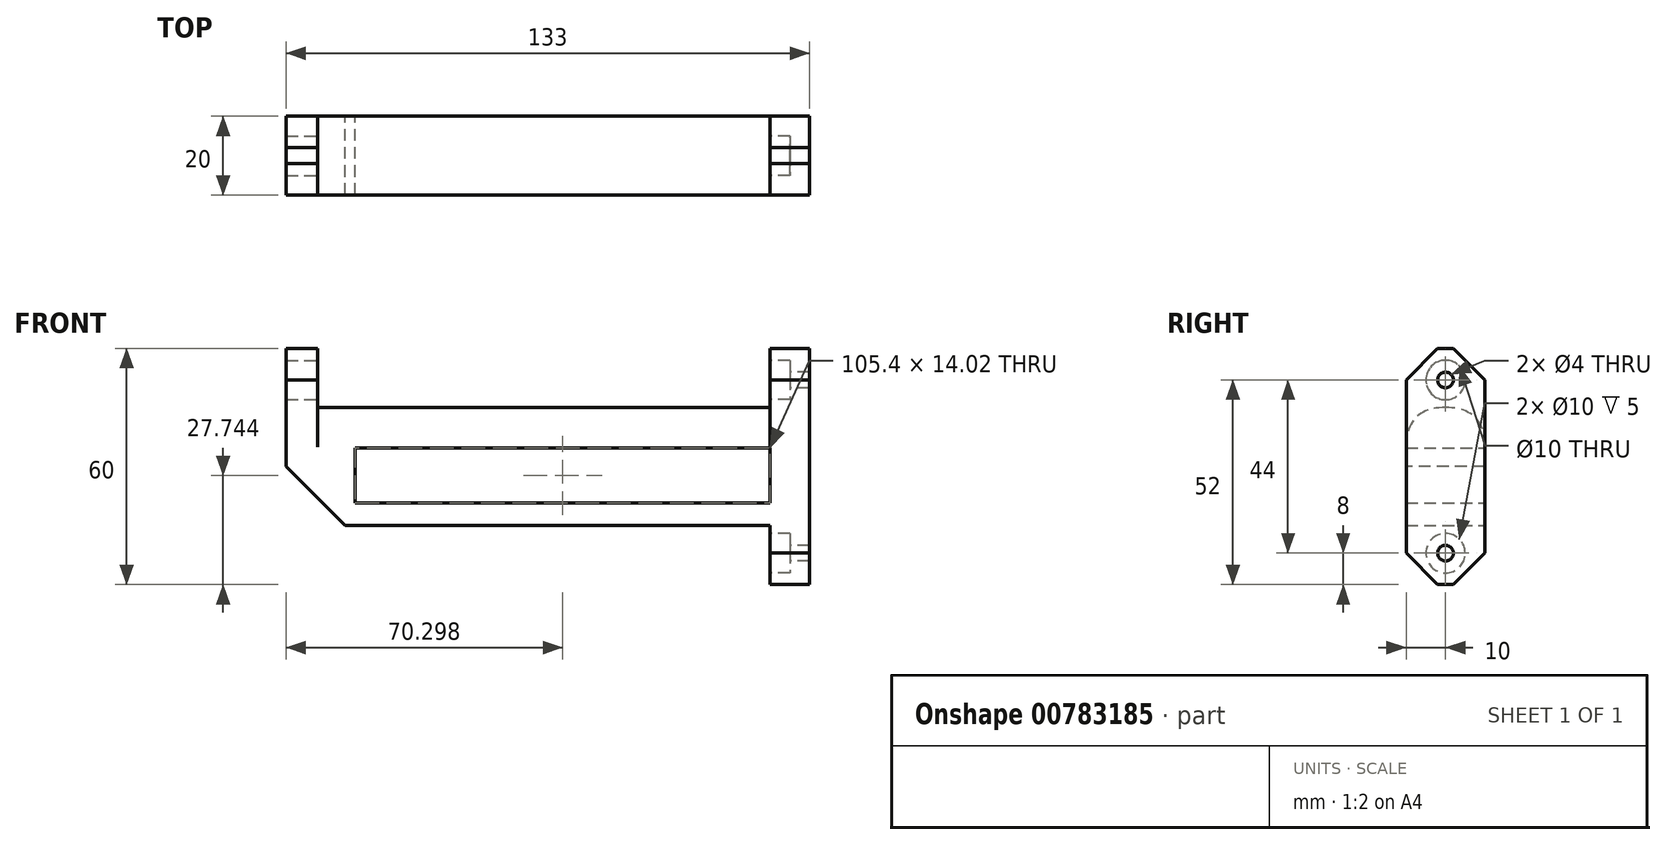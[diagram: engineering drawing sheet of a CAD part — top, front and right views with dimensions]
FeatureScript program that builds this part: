
annotation { "Feature Type Name" : "Feature", "Feature Type Description" : "" }
export const myFeature = defineFeature(function(context is Context, id is Id, definition is map)
    precondition{}
    {
        {
            var Q0;
            Q0=qCreatedBy(makeId("Front.planeOp"),FACE);
            var sketch = newSketch(context, id + "F0", { "sketchPlane" : qUnion([Q0])});
            skLineSegment(sketch, "E0.bottom", {"start": v(57.5, 15) * mm, "end": v(-57.5, 15) * mm});
            skLineSegment(sketch, "E0.top", {"start": v(57.5, -15) * mm, "end": v(-57.5, -15) * mm});
            skLineSegment(sketch, "E0.left", {"start": v(57.5, 15) * mm, "end": v(57.5, -15) * mm});
            skLineSegment(sketch, "E0.right", {"start": v(-57.5, 15) * mm, "end": v(-57.5, -15) * mm});
            skPoint(sketch, "E0.middle", {"position": v(0, 0) * mm});
            skLineSegment(sketch, "E1.bottom", {"start": v(-57.5, -15) * mm, "end": v(-65.5, -15) * mm});
            skLineSegment(sketch, "E1.top", {"start": v(-57.5, 30) * mm, "end": v(-65.5, 30) * mm});
            skLineSegment(sketch, "E1.left", {"start": v(-57.5, -15) * mm, "end": v(-57.5, 30) * mm});
            skLineSegment(sketch, "E1.right", {"start": v(-65.5, -15) * mm, "end": v(-65.5, 30) * mm});
            skLineSegment(sketch, "E2", {"start": v(57.5, 15) * mm, "end": v(57.5, 30) * mm});
            skLineSegment(sketch, "E3", {"start": v(57.5, 30) * mm, "end": v(67.5, 30) * mm});
            skLineSegment(sketch, "E4", {"start": v(67.5, 30) * mm, "end": v(67.5, 15) * mm});
            skLineSegment(sketch, "E5", {"start": v(67.5, 15) * mm, "end": v(67.5, -15) * mm});
            skLineSegment(sketch, "E6", {"start": v(67.5, -15) * mm, "end": v(67.5, -30) * mm});
            skLineSegment(sketch, "E7", {"start": v(67.5, -30) * mm, "end": v(57.5, -30) * mm});
            skLineSegment(sketch, "E8", {"start": v(57.5, -30) * mm, "end": v(57.5, -15) * mm});
            skLineSegment(sketch, "E9.bottom", {"start": v(57.5, -9.26) * mm, "end": v(-47.9, -9.26) * mm});
            skLineSegment(sketch, "E9.top", {"start": v(57.5, 4.75) * mm, "end": v(-47.9, 4.75) * mm});
            skLineSegment(sketch, "E9.left", {"start": v(57.5, -9.26) * mm, "end": v(57.5, 4.75) * mm});
            skLineSegment(sketch, "E9.right", {"start": v(-47.9, -9.26) * mm, "end": v(-47.9, 4.75) * mm});
            skSolve(sketch);
        }
        {
            var Q0;
            Q0 = qSketchRegion(id + "F0", true);
            extrude(context, id + "F1", {"entities" : qUnion([Q0]), "endBound" : BoundingType.SYMMETRIC, "depth" : 20 * mm, "offsetDistance" : 25 * mm});
        }
        {
            var Q0;
            Q0=makeQuery(id+"F1.opExtrude","CAP_EDGE",EDGE,{"disambiguationData":[OSD([sQuery(id+"F0.wireOp",EDGE,"E0.bottom")])],"isStart":false});
            var Q1;
            Q1=makeQuery(id+"F1.opExtrude","CAP_EDGE",EDGE,{"disambiguationData":[OSD([sQuery(id+"F0.wireOp",EDGE,"E0.bottom")])],"isStart":true});
            fillet(context, id + "F2", {"entities" : qUnion([Q0, Q1]), "radius" : 10 * mm, "rho" : 0.5, "crossSection" : FilletCrossSection.CONIC, "allowEdgeOverflow" : false});
        }
        {
            var Q0;
            Q0=makeQuery(id+"F1.opExtrude","CAP_EDGE",EDGE,{"disambiguationData":[OSD([sQuery(id+"F0.wireOp",EDGE,"E7")])],"isStart":false});
            var Q1;
            Q1=makeQuery(id+"F1.opExtrude","CAP_EDGE",EDGE,{"disambiguationData":[OSD([sQuery(id+"F0.wireOp",EDGE,"E7")])],"isStart":true});
            var Q2;
            Q2=makeQuery(id+"F1.opExtrude","CAP_EDGE",EDGE,{"disambiguationData":[OSD([sQuery(id+"F0.wireOp",EDGE,"E3")])],"isStart":true});
            var Q3;
            Q3=makeQuery(id+"F1.opExtrude","CAP_EDGE",EDGE,{"disambiguationData":[OSD([sQuery(id+"F0.wireOp",EDGE,"E3")])],"isStart":false});
            var Q4;
            Q4=makeQuery(id+"F1.opExtrude","CAP_EDGE",EDGE,{"disambiguationData":[OSD([sQuery(id+"F0.wireOp",EDGE,"E1.top")])],"isStart":false});
            var Q5;
            Q5=makeQuery(id+"F1.opExtrude","CAP_EDGE",EDGE,{"disambiguationData":[OSD([sQuery(id+"F0.wireOp",EDGE,"E1.top")])],"isStart":true});
            chamfer(context, id + "F3", {"entities" : qUnion([Q0, Q1, Q2, Q3, Q4, Q5]), "width" : 8 * mm, "tangentPropagation" : true});
        }
        {
            var Q0;
            Q0=makeQuery(id+"F1.opExtrude","SWEPT_FACE",FACE,{"disambiguationData":[OSD([sQuery(id+"F0.wireOp",EDGE,"E2")])]});
            var sketch = newSketch(context, id + "F4", { "sketchPlane" : qUnion([Q0])});
            skPoint(sketch, "E10", {"position": v(0, 22) * mm});
            skSolve(sketch);
        }
        {
            var Q0;
            Q0=sQuery(id+"F4.wireOp",VERTEX,"E10");
            var Q1;
            Q1=makeQuery(id+"F1.opExtrude","SWEPT_BODY",BODY,{"disambiguationData":[OSD([sQuery(id+"F0.wireOp",EDGE,"E0.bottom"),sQuery(id+"F0.wireOp",EDGE,"E0.top"),sQuery(id+"F0.wireOp",EDGE,"E1.bottom"),sQuery(id+"F0.wireOp",EDGE,"E1.top"),sQuery(id+"F0.wireOp",EDGE,"E1.left"),sQuery(id+"F0.wireOp",EDGE,"E1.right"),sQuery(id+"F0.wireOp",EDGE,"E2"),sQuery(id+"F0.wireOp",EDGE,"E3"),sQuery(id+"F0.wireOp",EDGE,"E4"),sQuery(id+"F0.wireOp",EDGE,"E5"),sQuery(id+"F0.wireOp",EDGE,"E6"),sQuery(id+"F0.wireOp",EDGE,"E7"),sQuery(id+"F0.wireOp",EDGE,"E8")])]});
            hole(context, id + "F5", {"style" : HoleStyle.C_BORE, "endStyle" : HoleEndStyle.BLIND, "holeDiameter" : 4 * mm, "cBoreDiameter" : 10 * mm, "cBoreDepth" : 5 * mm, "majorDiameter" : 5 * mm, "holeDepth" : 12 * mm, "isTappedThrough" : true, "tappedDepth" : 12 * mm, "tapClearance" : 3, "locations" : qUnion([Q0]), "scope" : qUnion([Q1])});
        }
        {
            var Q0;
            Q0=makeQuery(id+"F1.opExtrude","SWEPT_FACE",FACE,{"disambiguationData":[OSD([sQuery(id+"F0.wireOp",EDGE,"E8")])]});
            var sketch = newSketch(context, id + "F6", { "sketchPlane" : qUnion([Q0])});
            skPoint(sketch, "E11", {"position": v(0, -22) * mm});
            skSolve(sketch);
        }
        {
            var Q0;
            Q0=sQuery(id+"F6.wireOp",VERTEX,"E11");
            var Q1;
            Q1=makeQuery(id+"F1.opExtrude","SWEPT_BODY",BODY,{"disambiguationData":[OSD([sQuery(id+"F0.wireOp",EDGE,"E0.bottom"),sQuery(id+"F0.wireOp",EDGE,"E0.top"),sQuery(id+"F0.wireOp",EDGE,"E1.bottom"),sQuery(id+"F0.wireOp",EDGE,"E1.top"),sQuery(id+"F0.wireOp",EDGE,"E1.left"),sQuery(id+"F0.wireOp",EDGE,"E1.right"),sQuery(id+"F0.wireOp",EDGE,"E2"),sQuery(id+"F0.wireOp",EDGE,"E3"),sQuery(id+"F0.wireOp",EDGE,"E4"),sQuery(id+"F0.wireOp",EDGE,"E5"),sQuery(id+"F0.wireOp",EDGE,"E6"),sQuery(id+"F0.wireOp",EDGE,"E7"),sQuery(id+"F0.wireOp",EDGE,"E8")])]});
            hole(context, id + "F7", {"style" : HoleStyle.C_BORE, "endStyle" : HoleEndStyle.BLIND, "holeDiameter" : 4 * mm, "cBoreDiameter" : 10 * mm, "cBoreDepth" : 5 * mm, "majorDiameter" : 5 * mm, "holeDepth" : 12 * mm, "isTappedThrough" : true, "tappedDepth" : 12 * mm, "tapClearance" : 3, "locations" : qUnion([Q0]), "scope" : qUnion([Q1])});
        }
        {
            var Q0;
            Q0=makeQuery(id+"F1.opExtrude","SWEPT_EDGE",EDGE,{"disambiguationData":[OSD([sQuery(id+"F0.wireOp",EDGE,"E1.bottom"),sQuery(id+"F0.wireOp",EDGE,"E1.right")])]});
            chamfer(context, id + "F8", {"entities" : qUnion([Q0]), "width" : 15 * mm, "tangentPropagation" : true});
        }
        {
            var Q0;
            Q0=makeQuery(id+"F1.opExtrude","SWEPT_FACE",FACE,{"disambiguationData":[OSD([sQuery(id+"F0.wireOp",EDGE,"E1.left")])]});
            var sketch = newSketch(context, id + "F9", { "sketchPlane" : qUnion([Q0])});
            skCircle(sketch, "E12", {"center": v(0, 22) * mm, "radius": 5 * mm});
            skSolve(sketch);
        }
        {
            var Q0;
            Q0=makeQuery(id+"F9.imprint","IMPRINT",FACE,{"disambiguationData":[TD([[makeQuery(id+"F9.imprint","IMPRINT",EDGE,{"derivedFrom":sQuery(id+"F9.wireOp",EDGE,"E12")}),1.0]])]});
            extrude(context, id + "F10", {"entities" : qUnion([Q0]), "operationType" : NewBodyOperationType.REMOVE, "oppositeDirection" : true, "depth" : 25 * mm, "offsetDistance" : 25 * mm});
        }
    });
